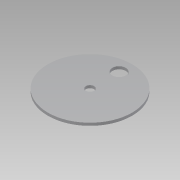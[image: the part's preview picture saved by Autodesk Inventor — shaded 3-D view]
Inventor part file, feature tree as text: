
AUTODESK INVENTOR PART (.ipt)
format: ipt  version: 2015 (Build 190159000, 159)  size: 79,872 bytes
history: native  units: mm
features: extrude x1, sketch x1
ambient origin geometry x8: Origin, YZ Plane, XZ Plane, XY Plane, X Axis, Y Axis, Z Axis, Center Point
bodies: Body1 (feature_tree)
feature tree (2):
  extrude  "Extrusion2"  Depth=3.0mm
  sketch  "Sketch1"  dims[d0=94.0mm d1=9.18mm d4=15.0mm d5=32.5mm d6=3.0mm d7=0.0mm]
